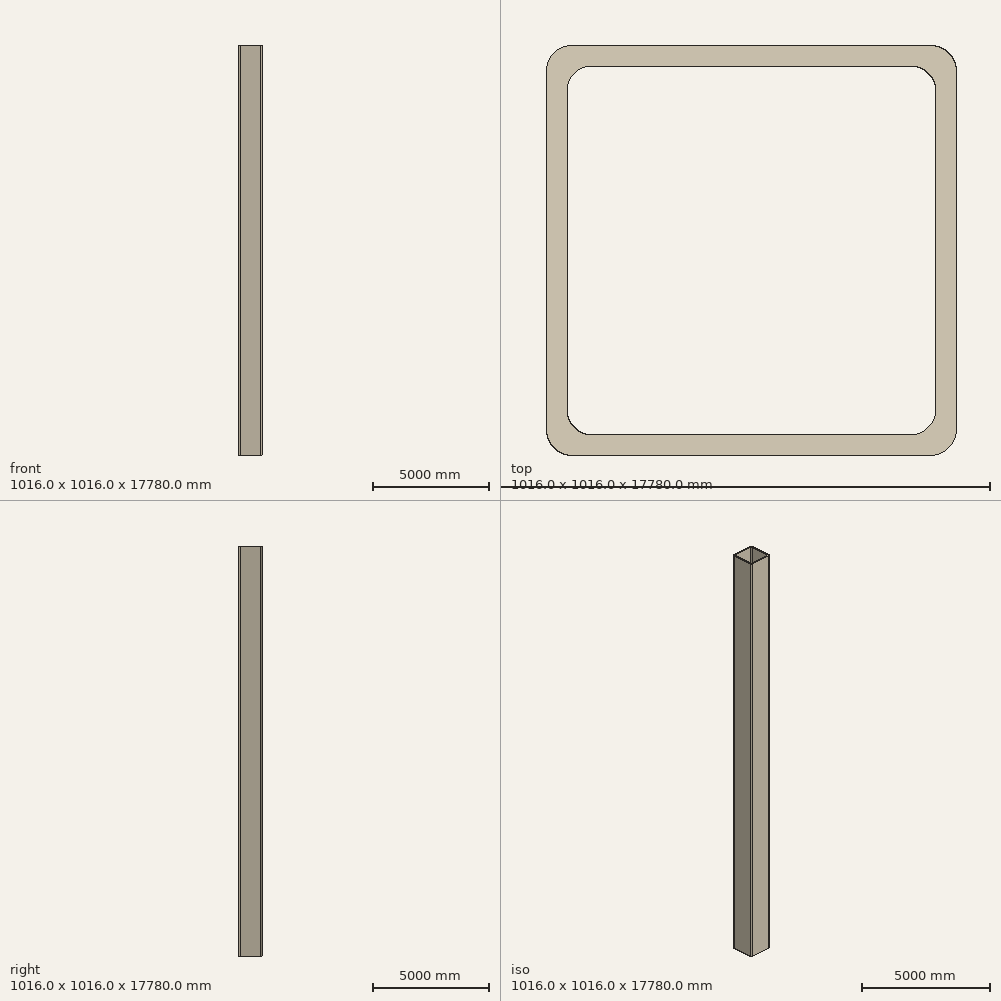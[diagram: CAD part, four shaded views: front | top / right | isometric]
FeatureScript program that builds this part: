
annotation { "Feature Type Name" : "Feature", "Feature Type Description" : "" }
export const myFeature = defineFeature(function(context is Context, id is Id, definition is map)
    precondition{}
    {
        {
            var Q0;
            Q0=qCreatedBy(makeId("Top.planeOp"),FACE);
            var sketch = newSketch(context, id + "F0", { "sketchPlane" : qUnion([Q0])});
            skLineSegment(sketch, "E0.bottom", {"start": v(-445.9, 501.34) * mm, "end": v(443.1, 501.34) * mm});
            skLineSegment(sketch, "E0.top", {"start": v(-445.9, -514.66) * mm, "end": v(443.1, -514.66) * mm});
            skLineSegment(sketch, "E0.left", {"start": v(-509.4, 437.84) * mm, "end": v(-509.4, -451.16) * mm});
            skLineSegment(sketch, "E0.right", {"start": v(506.6, 437.84) * mm, "end": v(506.6, -451.16) * mm});
            skLineSegment(sketch, "E1.bottom", {"start": v(-395.1, 450.54) * mm, "end": v(392.3, 450.54) * mm});
            skLineSegment(sketch, "E1.top", {"start": v(-395.1, -463.86) * mm, "end": v(392.3, -463.86) * mm});
            skLineSegment(sketch, "E1.left", {"start": v(-458.6, 387.04) * mm, "end": v(-458.6, -400.36) * mm});
            skLineSegment(sketch, "E1.right", {"start": v(455.8, 387.04) * mm, "end": v(455.8, -400.36) * mm});
            skPoint(sketch, "E2.visualSharp", {"position": v(506.6, 501.34) * mm});
            skArc(sketch, "E2.filletArc", {"start": v(506.6, 437.84) * mm, "mid": v(488, 482.74) * mm, "end": v(443.1, 501.34) * mm});
            skPoint(sketch, "E3.visualSharp", {"position": v(-509.4, 501.34) * mm});
            skArc(sketch, "E3.filletArc", {"start": v(-445.9, 501.34) * mm, "mid": v(-490.8, 482.74) * mm, "end": v(-509.4, 437.84) * mm});
            skPoint(sketch, "E4.visualSharp", {"position": v(506.6, -514.66) * mm});
            skArc(sketch, "E4.filletArc", {"start": v(443.1, -514.66) * mm, "mid": v(488, -496.07) * mm, "end": v(506.6, -451.16) * mm});
            skPoint(sketch, "E5.visualSharp", {"position": v(-509.4, -514.66) * mm});
            skArc(sketch, "E5.filletArc", {"start": v(-509.4, -451.16) * mm, "mid": v(-490.8, -496.07) * mm, "end": v(-445.9, -514.66) * mm});
            skPoint(sketch, "E6.visualSharp", {"position": v(455.8, -463.86) * mm});
            skArc(sketch, "E6.filletArc", {"start": v(392.3, -463.86) * mm, "mid": v(437.2, -445.27) * mm, "end": v(455.8, -400.36) * mm});
            skPoint(sketch, "E7.visualSharp", {"position": v(-458.6, -463.86) * mm});
            skArc(sketch, "E7.filletArc", {"start": v(-458.6, -400.36) * mm, "mid": v(-440, -445.27) * mm, "end": v(-395.1, -463.86) * mm});
            skPoint(sketch, "E8.visualSharp", {"position": v(455.8, 450.54) * mm});
            skArc(sketch, "E8.filletArc", {"start": v(455.8, 387.04) * mm, "mid": v(437.2, 431.94) * mm, "end": v(392.3, 450.54) * mm});
            skPoint(sketch, "E9.visualSharp", {"position": v(-458.6, 450.54) * mm});
            skArc(sketch, "E9.filletArc", {"start": v(-395.1, 450.54) * mm, "mid": v(-440, 431.94) * mm, "end": v(-458.6, 387.04) * mm});
            skSolve(sketch);
        }
        {
            var Q0;
            Q0 = qSketchRegion(id + "F0", true);
            extrude(context, id + "F1", {"entities" : qUnion([Q0]), "depth" : 17780 * mm, "offsetDistance" : 25.4 * mm});
        }
    });
